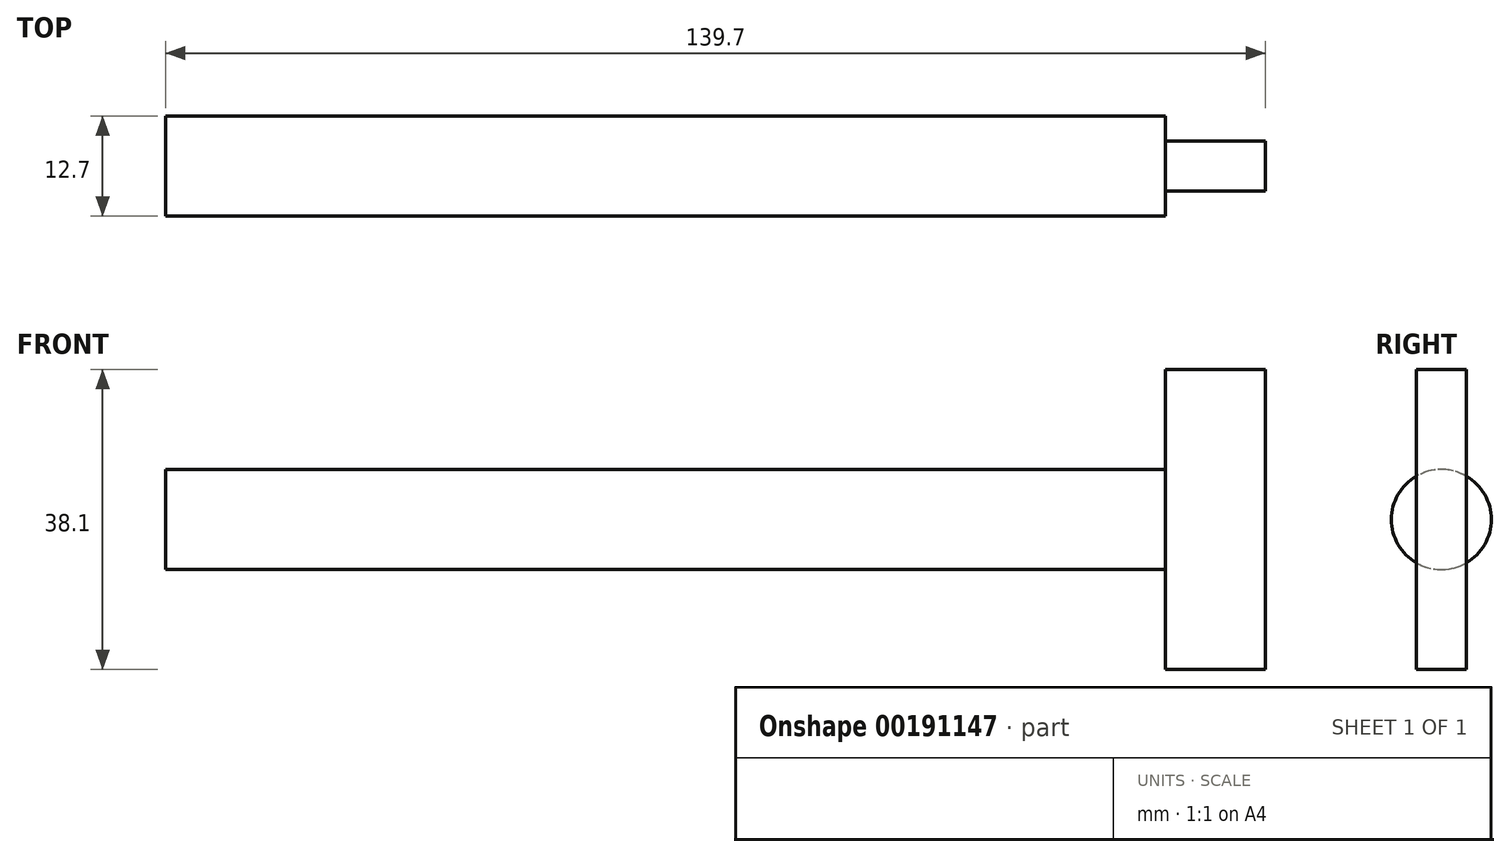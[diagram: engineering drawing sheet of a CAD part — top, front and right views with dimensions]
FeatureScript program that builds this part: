
annotation { "Feature Type Name" : "Feature", "Feature Type Description" : "" }
export const myFeature = defineFeature(function(context is Context, id is Id, definition is map)
    precondition{}
    {
        {
            var Q0;
            Q0=qCreatedBy(makeId("Right.planeOp"),FACE);
            var sketch = newSketch(context, id + "F0", { "sketchPlane" : qUnion([Q0])});
            skCircle(sketch, "E0", {"center": v(0, 0) * mm, "radius": 6.35 * mm});
            skSolve(sketch);
        }
        {
            var Q0;
            Q0 = qSketchRegion(id + "F0", true);
            extrude(context, id + "F1", {"entities" : qUnion([Q0]), "depth" : 127 * mm});
        }
        {
            var Q0;
            Q0=qCreatedBy(makeId("Front.planeOp"),FACE);
            var sketch = newSketch(context, id + "F2", { "sketchPlane" : qUnion([Q0])});
            skLineSegment(sketch, "E1.bottom", {"start": v(127, 19.05) * mm, "end": v(139.7, 19.05) * mm});
            skLineSegment(sketch, "E1.top", {"start": v(127, -19.05) * mm, "end": v(139.7, -19.05) * mm});
            skLineSegment(sketch, "E1.left", {"start": v(127, 19.05) * mm, "end": v(127, -19.05) * mm});
            skLineSegment(sketch, "E1.right", {"start": v(139.7, 19.05) * mm, "end": v(139.7, -19.05) * mm});
            skPoint(sketch, "E2", {"position": v(127, 0) * mm});
            skSolve(sketch);
        }
        {
            var Q0;
            Q0 = qSketchRegion(id + "F2", true);
            extrude(context, id + "F3", {"entities" : qUnion([Q0]), "operationType" : NewBodyOperationType.ADD, "endBound" : BoundingType.SYMMETRIC, "depth" : 6.35 * mm});
        }
    });
